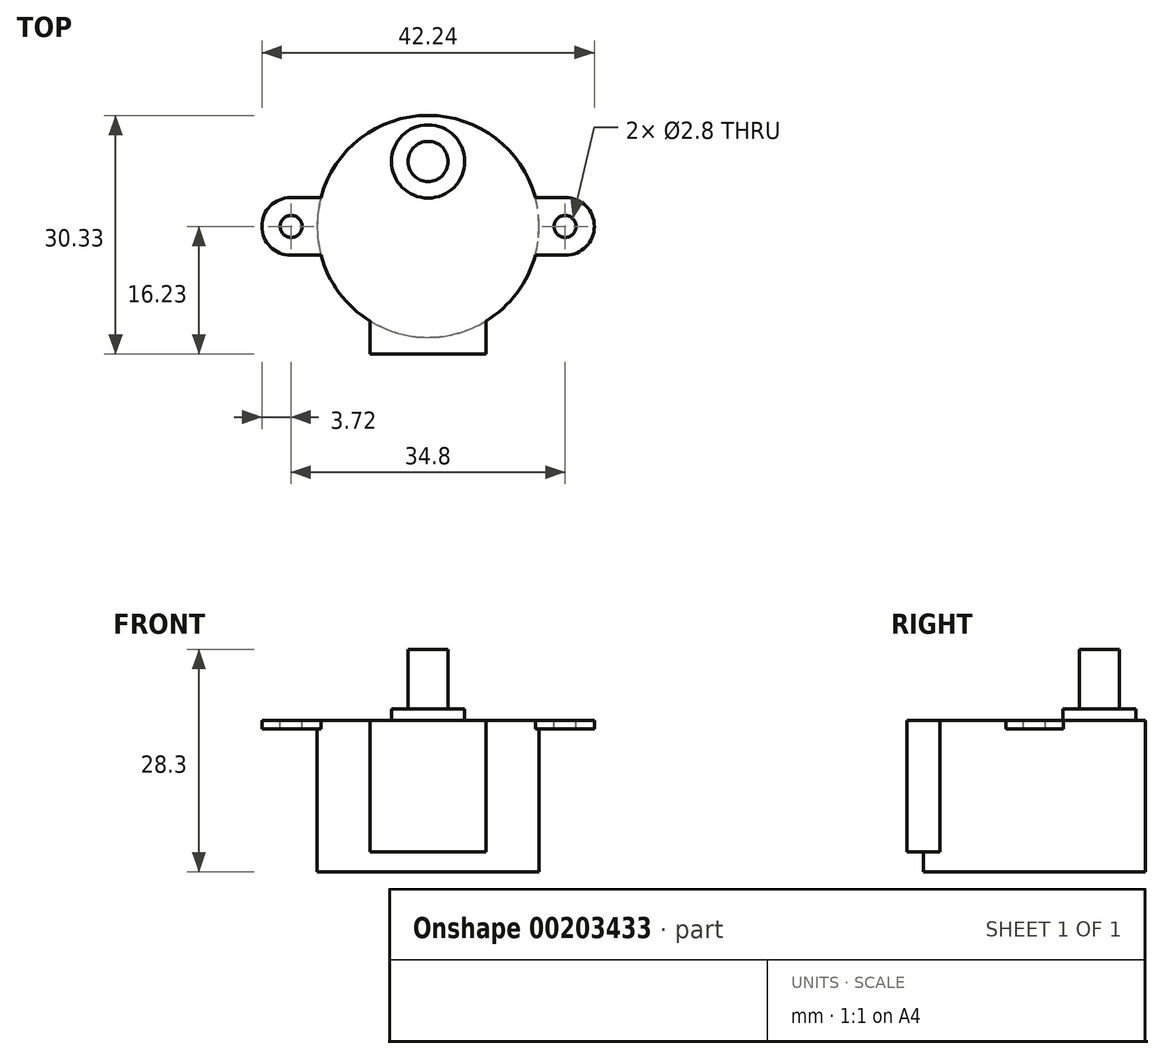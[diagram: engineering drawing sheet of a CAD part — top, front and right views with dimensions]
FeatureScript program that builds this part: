
annotation { "Feature Type Name" : "Feature", "Feature Type Description" : "" }
export const myFeature = defineFeature(function(context is Context, id is Id, definition is map)
    precondition{}
    {
        {
            var Q0;
            Q0=qCreatedBy(makeId("Top.planeOp"),FACE);
            var sketch = newSketch(context, id + "F0", { "sketchPlane" : qUnion([Q0])});
            skCircle(sketch, "E0", {"center": v(0, 0) * mm, "radius": 14.1 * mm});
            skCircle(sketch, "E1", {"center": v(0, 8.25) * mm, "radius": 4.65 * mm});
            skLineSegment(sketch, "E2.bottom", {"start": v(-7.35, -12.03) * mm, "end": v(7.35, -12.03) * mm});
            skLineSegment(sketch, "E2.top", {"start": v(-7.35, -16.23) * mm, "end": v(7.35, -16.23) * mm});
            skLineSegment(sketch, "E2.left", {"start": v(-7.35, -12.03) * mm, "end": v(-7.35, -16.23) * mm});
            skLineSegment(sketch, "E2.right", {"start": v(7.35, -12.03) * mm, "end": v(7.35, -16.23) * mm});
            skPoint(sketch, "E3", {"position": v(0, -16.23) * mm});
            skCircle(sketch, "E4", {"center": v(0, 8.25) * mm, "radius": 2.55 * mm});
            skLineSegment(sketch, "E5.bottom", {"start": v(13.62, 3.65) * mm, "end": v(17.47, 3.65) * mm});
            skLineSegment(sketch, "E5.top", {"start": v(13.62, -3.65) * mm, "end": v(17.47, -3.65) * mm});
            skLineSegment(sketch, "E5.left", {"start": v(13.62, 3.65) * mm, "end": v(13.62, -3.65) * mm});
            skLineSegment(sketch, "E5.right", {"start": v(21.12, 0) * mm, "end": v(21.12, 0) * mm});
            skPoint(sketch, "E6.visualSharp", {"position": v(21.12, 3.65) * mm});
            skArc(sketch, "E6.filletArc", {"start": v(21.12, 0) * mm, "mid": v(20.05, 2.58) * mm, "end": v(17.47, 3.65) * mm});
            skPoint(sketch, "E7.visualSharp", {"position": v(21.12, -3.65) * mm});
            skArc(sketch, "E7.filletArc", {"start": v(17.47, -3.65) * mm, "mid": v(20.05, -2.58) * mm, "end": v(21.12, 0) * mm});
            skCircle(sketch, "E8", {"center": v(17.4, 0) * mm, "radius": 1.4 * mm});
            skLineSegment(sketch, "E9.MirrorCS", {"start": v(-13.62, 3.65) * mm, "end": v(-17.47, 3.65) * mm});
            skArc(sketch, "E10.MirrorCS", {"start": v(-21.12, 0) * mm, "mid": v(-20.05, 2.58) * mm, "end": v(-17.47, 3.65) * mm});
            skArc(sketch, "E11.MirrorCS", {"start": v(-17.47, -3.65) * mm, "mid": v(-20.05, -2.58) * mm, "end": v(-21.12, 0) * mm});
            skLineSegment(sketch, "E12.MirrorCS", {"start": v(-13.62, -3.65) * mm, "end": v(-17.47, -3.65) * mm});
            skCircle(sketch, "E13.MirrorC", {"center": v(-17.4, 0) * mm, "radius": 1.4 * mm});
            skPoint(sketch, "E14", {"position": v(0, 3.6) * mm});
            skSolve(sketch);
        }
        {
            var Q0;
            Q0=makeQuery(id+"F0.imprint","IMPRINT",FACE,{"disambiguationData":[TD([[makeQuery(id+"F0.imprint","IMPRINT",EDGE,{"derivedFrom":sQuery(id+"F0.wireOp",EDGE,"E1")}),1.0]])]});
            extrude(context, id + "F1", {"entities" : qUnion([Q0]), "depth" : 1.4 * mm});
        }
        {
            var Q0;
            Q0=makeQuery(id+"F0.imprint","IMPRINT",FACE,{"disambiguationData":[TD([[makeQuery(id+"F0.imprint","IMPRINT",EDGE,{"derivedFrom":sQuery(id+"F0.wireOp",EDGE,"E4")}),1.0]])]});
            extrude(context, id + "F2", {"entities" : qUnion([Q0]), "operationType" : NewBodyOperationType.ADD, "depth" : 9 * mm});
        }
        {
            var Q0;
            {var subQ0=sQuery(id+"F0.wireOp",EDGE,"E2.bottom");Q0=makeQuery(id+"F0.imprint","IMPRINT",FACE,{"disambiguationData":[TD([[makeQuery(id+"F0.imprint","IMPRINT",EDGE,{"derivedFrom":subQ0}),-1.0]])]});}
            var Q1;
            Q1=makeQuery(id+"F0.imprint","IMPRINT",FACE,{"disambiguationData":[TD([[makeQuery(id+"F0.imprint","IMPRINT",EDGE,{"derivedFrom":sQuery(id+"F0.wireOp",EDGE,"E1")}),-1.0]])]});
            var Q2;
            Q2=makeQuery(id+"F0.imprint","IMPRINT",FACE,{"disambiguationData":[TD([[makeQuery(id+"F0.imprint","IMPRINT",EDGE,{"derivedFrom":sQuery(id+"F0.wireOp",EDGE,"E1")}),1.0]])]});
            var Q3;
            Q3=makeQuery(id+"F0.imprint","IMPRINT",FACE,{"disambiguationData":[TD([[makeQuery(id+"F0.imprint","IMPRINT",EDGE,{"derivedFrom":sQuery(id+"F0.wireOp",EDGE,"E4")}),1.0]])]});
            var Q4;
            {var subQ0=sQuery(id+"F0.wireOp",EDGE,"E5.left");Q4=makeQuery(id+"F0.imprint","IMPRINT",FACE,{"disambiguationData":[TD([[makeQuery(id+"F0.imprint","IMPRINT",EDGE,{"derivedFrom":subQ0}),1.0]])]});}
            var Q5;
            Q5 = qConstructionFilter(qBodyType(qCreatedBy(id + "F0" ,EDGE), BodyType.WIRE), ConstructionObject.NO);
            extrude(context, id + "F3", {"entities" : qUnion([Q0, Q1, Q2, Q3, Q4]), "operationType" : NewBodyOperationType.ADD, "surfaceEntities" : qUnion([Q5]), "oppositeDirection" : true, "depth" : 19.3 * mm});
        }
        {
            var Q0;
            Q0=makeQuery(id+"F0.imprint","IMPRINT",FACE,{"disambiguationData":[TD([[makeQuery(id+"F0.imprint","IMPRINT",EDGE,{"derivedFrom":sQuery(id+"F0.wireOp",EDGE,"E2.top")}),1.0]])]});
            extrude(context, id + "F4", {"entities" : qUnion([Q0]), "operationType" : NewBodyOperationType.ADD, "oppositeDirection" : true, "depth" : 16.7 * mm});
        }
        {
            var Q0;
            {var subQ0=sQuery(id+"F0.wireOp",EDGE,"E9.MirrorCS");Q0=makeQuery(id+"F0.imprint","IMPRINT",FACE,{"disambiguationData":[TD([[makeQuery(id+"F0.imprint","IMPRINT",EDGE,{"derivedFrom":subQ0}),1.0]])]});}
            var Q1;
            {var subQ1=sQuery(id+"F0.wireOp",EDGE,"E5.bottom");Q1=makeQuery(id+"F0.imprint","IMPRINT",FACE,{"disambiguationData":[TD([[makeQuery(id+"F0.imprint","IMPRINT",EDGE,{"derivedFrom":subQ1}),-1.0]])]});}
            extrude(context, id + "F5", {"entities" : qUnion([Q0, Q1]), "operationType" : NewBodyOperationType.ADD, "oppositeDirection" : true, "depth" : 1.1 * mm});
        }
    });
